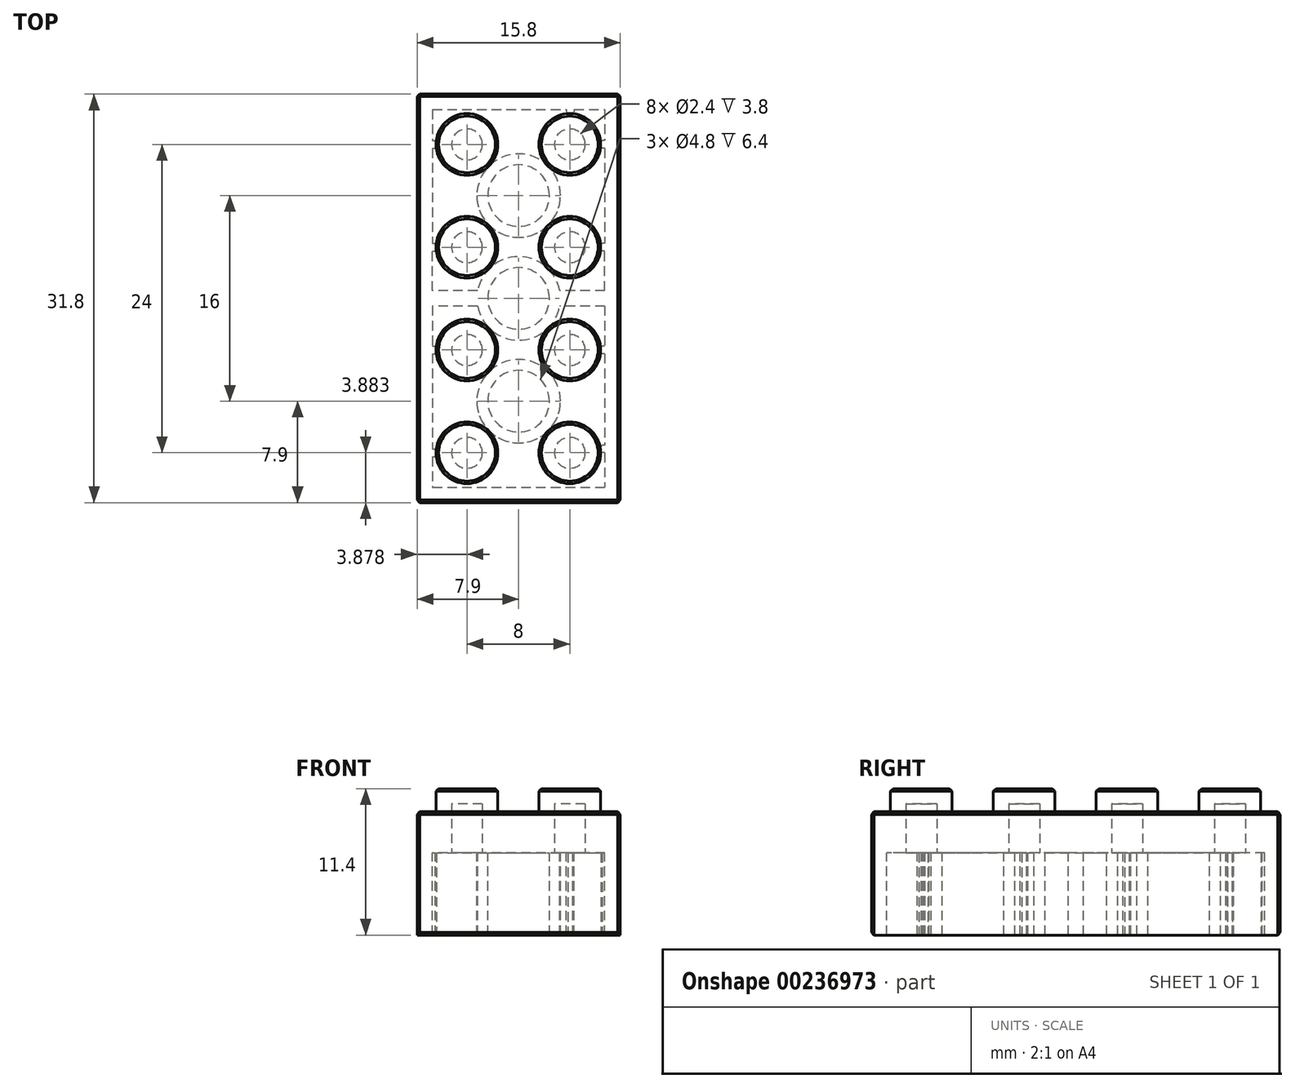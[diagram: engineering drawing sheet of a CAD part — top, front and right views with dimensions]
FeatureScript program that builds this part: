
annotation { "Feature Type Name" : "Feature", "Feature Type Description" : "" }
export const myFeature = defineFeature(function(context is Context, id is Id, definition is map)
    precondition{}
    {
        {
            var Q0;
            Q0=qCreatedBy(makeId("Top.planeOp"),FACE);
            var sketch = newSketch(context, id + "F0", { "sketchPlane" : qUnion([Q0])});
            skLineSegment(sketch, "E0.bottom", {"start": v(-7.9, 15.9) * mm, "end": v(7.9, 15.9) * mm});
            skLineSegment(sketch, "E0.top", {"start": v(-7.9, -15.9) * mm, "end": v(7.9, -15.9) * mm});
            skLineSegment(sketch, "E0.left", {"start": v(-7.9, 15.9) * mm, "end": v(-7.9, -15.9) * mm});
            skLineSegment(sketch, "E0.right", {"start": v(7.9, 15.9) * mm, "end": v(7.9, -15.9) * mm});
            skPoint(sketch, "E0.middle", {"position": v(0, 0) * mm});
            skSolve(sketch);
        }
        {
            var Q0;
            Q0=qCreatedBy(makeId("Top.planeOp"),FACE);
            var sketch = newSketch(context, id + "F1", { "sketchPlane" : qUnion([Q0])});
            skCircle(sketch, "E1", {"center": v(-4.02, 11.98) * mm, "radius": 2.4 * mm});
            skCircle(sketch, "E2", {"center": v(-4.02, 3.98) * mm, "radius": 2.4 * mm});
            skCircle(sketch, "E3", {"center": v(-4.02, -4.02) * mm, "radius": 2.4 * mm});
            skCircle(sketch, "E4", {"center": v(-4.02, -12.02) * mm, "radius": 2.4 * mm});
            skCircle(sketch, "E5", {"center": v(3.98, -12.02) * mm, "radius": 2.4 * mm});
            skCircle(sketch, "E6", {"center": v(3.98, -4.02) * mm, "radius": 2.4 * mm});
            skCircle(sketch, "E7", {"center": v(3.98, 3.98) * mm, "radius": 2.4 * mm});
            skCircle(sketch, "E8", {"center": v(3.98, 11.98) * mm, "radius": 2.4 * mm});
            skLineSegment(sketch, "E9", {"start": v(-4.02, 3.98) * mm, "end": v(3.98, 3.98) * mm});
            skLineSegment(sketch, "E10", {"start": v(0, 3.98) * mm, "end": v(0, 11.98) * mm});
            skSolve(sketch);
        }
        {
            var Q0;
            Q0=makeQuery(id+"F0.imprint","IMPRINT",FACE,{"disambiguationData":[TD([[makeQuery(id+"F0.imprint","IMPRINT",EDGE,{"derivedFrom":sQuery(id+"F0.wireOp",EDGE,"E0.bottom")}),-1.0]])]});
            extrude(context, id + "F2", {"entities" : qUnion([Q0]), "oppositeDirection" : true, "depth" : 9.6 * mm});
        }
        {
            var Q0;
            Q0=makeQuery(id+"F1.imprint","IMPRINT",FACE,{"disambiguationData":[TD([[makeQuery(id+"F1.imprint","IMPRINT",EDGE,{"derivedFrom":sQuery(id+"F1.wireOp",EDGE,"E1")}),1.0]])]});
            extrude(context, id + "F3", {"entities" : qUnion([Q0]), "operationType" : NewBodyOperationType.ADD, "depth" : 1.8 * mm});
        }
        {
            var Q0;
            Q0 = qSketchRegion(id + "F1", true);
            extrude(context, id + "F4", {"entities" : qUnion([Q0]), "operationType" : NewBodyOperationType.ADD, "depth" : 1.8 * mm});
        }
        {
            var Q0;
            Q0=makeQuery(id+"F2.opExtrude","CAP_FACE",FACE,{"disambiguationData":[OSD([sQuery(id+"F0.wireOp",EDGE,"E0.bottom"),sQuery(id+"F0.wireOp",EDGE,"E0.top"),sQuery(id+"F0.wireOp",EDGE,"E0.left"),sQuery(id+"F0.wireOp",EDGE,"E0.right")])],"isStart":false});
            shell(context, id + "F5", {"entities" : qUnion([Q0]), "thickness" : 1.2 * mm});
        }
        {
            var Q0;
            Q0=makeQuery(id+"F5.opShell","OFFSET_FACE",FACE,{"disambiguationData":[OSD([sQuery(id+"F0.wireOp",EDGE,"E0.bottom"),sQuery(id+"F0.wireOp",EDGE,"E0.top"),sQuery(id+"F0.wireOp",EDGE,"E0.left"),sQuery(id+"F0.wireOp",EDGE,"E0.right")])]});
            extrude(context, id + "F6", {"entities" : qUnion([Q0]), "operationType" : NewBodyOperationType.ADD, "depth" : 2 * mm});
        }
        {
            var Q0;
            Q0=makeQuery(id+"F6.opExtrude","CAP_FACE",FACE,{"disambiguationData":[OSD([sQuery(id+"F0.wireOp",EDGE,"E0.bottom"),sQuery(id+"F0.wireOp",EDGE,"E0.top"),sQuery(id+"F0.wireOp",EDGE,"E0.left"),sQuery(id+"F0.wireOp",EDGE,"E0.right")])],"isStart":false});
            var sketch = newSketch(context, id + "F7", { "sketchPlane" : qUnion([Q0])});
            skCircle(sketch, "E11", {"center": v(0, 8) * mm, "radius": 3.25 * mm});
            skCircle(sketch, "E12", {"center": v(0, 0) * mm, "radius": 3.25 * mm});
            skCircle(sketch, "E13", {"center": v(0, -8) * mm, "radius": 3.25 * mm});
            skCircle(sketch, "E14", {"center": v(0, 8) * mm, "radius": 2.4 * mm});
            skCircle(sketch, "E15", {"center": v(0, 0) * mm, "radius": 2.4 * mm});
            skCircle(sketch, "E16", {"center": v(0, -8) * mm, "radius": 2.4 * mm});
            skLineSegment(sketch, "E17", {"start": v(-6.7, -3.98) * mm, "end": v(-6.7, -3.68) * mm});
            skLineSegment(sketch, "E18", {"start": v(-6.7, -3.68) * mm, "end": v(-6.7, -3.98) * mm});
            skLineSegment(sketch, "E19", {"start": v(-6.7, -3.98) * mm, "end": v(-6.7, -4.28) * mm});
            skLineSegment(sketch, "E20", {"start": v(-6.7, 4.02) * mm, "end": v(-6.7, 4.32) * mm});
            skLineSegment(sketch, "E21", {"start": v(-6.7, 4.02) * mm, "end": v(-6.7, 3.72) * mm});
            skLineSegment(sketch, "E22", {"start": v(-6.7, 12.02) * mm, "end": v(-6.7, 11.72) * mm});
            skLineSegment(sketch, "E23", {"start": v(-6.7, -11.98) * mm, "end": v(-6.7, -11.68) * mm});
            skLineSegment(sketch, "E24", {"start": v(-6.7, -11.68) * mm, "end": v(-6.7, -12.28) * mm});
            skLineSegment(sketch, "E25", {"start": v(-3.98, -14.7) * mm, "end": v(-4.28, -14.7) * mm});
            skLineSegment(sketch, "E26", {"start": v(-3.98, -14.7) * mm, "end": v(4.02, -14.7) * mm});
            skLineSegment(sketch, "E27", {"start": v(4.02, -14.7) * mm, "end": v(3.72, -14.7) * mm});
            skLineSegment(sketch, "E28", {"start": v(3.72, -14.7) * mm, "end": v(4.02, -14.7) * mm});
            skLineSegment(sketch, "E29", {"start": v(6.7, -3.98) * mm, "end": v(6.7, -4.28) * mm});
            skLineSegment(sketch, "E30", {"start": v(6.7, -4.28) * mm, "end": v(6.7, -3.98) * mm});
            skLineSegment(sketch, "E31", {"start": v(6.7, -4.28) * mm, "end": v(6.7, -3.68) * mm});
            skLineSegment(sketch, "E32", {"start": v(6.7, -3.98) * mm, "end": v(6.7, 4.02) * mm});
            skLineSegment(sketch, "E33", {"start": v(6.7, 4.02) * mm, "end": v(6.7, 4.32) * mm});
            skLineSegment(sketch, "E34", {"start": v(6.7, 4.32) * mm, "end": v(6.7, 3.72) * mm});
            skLineSegment(sketch, "E35", {"start": v(6.7, 3.72) * mm, "end": v(6.7, 11.72) * mm});
            skLineSegment(sketch, "E36", {"start": v(6.7, 11.72) * mm, "end": v(6.4, 11.72) * mm});
            skLineSegment(sketch, "E37", {"start": v(6.7, 11.72) * mm, "end": v(6.7, 11.42) * mm});
            skLineSegment(sketch, "E38", {"start": v(6.7, 11.72) * mm, "end": v(6.7, 12.02) * mm});
            skLineSegment(sketch, "E39", {"start": v(-6.7, 14.7) * mm, "end": v(-3.98, 14.7) * mm});
            skLineSegment(sketch, "E40", {"start": v(-3.98, 14.7) * mm, "end": v(-3.68, 14.7) * mm});
            skLineSegment(sketch, "E41", {"start": v(-3.98, 14.7) * mm, "end": v(-4.28, 14.7) * mm});
            skLineSegment(sketch, "E42", {"start": v(-3.98, 14.7) * mm, "end": v(3.91, 14.7) * mm});
            skLineSegment(sketch, "E43", {"start": v(6.7, -11.98) * mm, "end": v(6.7, -11.68) * mm});
            skLineSegment(sketch, "E44", {"start": v(6.7, -11.98) * mm, "end": v(6.7, -12.28) * mm});
            skLineSegment(sketch, "E45", {"start": v(-6.7, 12.02) * mm, "end": v(-6.7, 12.32) * mm});
            skLineSegment(sketch, "E46.bottom", {"start": v(-6.7, 11.72) * mm, "end": v(-6.4, 11.72) * mm});
            skLineSegment(sketch, "E46.top", {"start": v(-6.7, 12.32) * mm, "end": v(-6.4, 12.32) * mm});
            skLineSegment(sketch, "E46.left", {"start": v(-6.7, 11.72) * mm, "end": v(-6.7, 12.32) * mm});
            skLineSegment(sketch, "E46.right", {"start": v(-6.4, 11.72) * mm, "end": v(-6.4, 12.32) * mm});
            skLineSegment(sketch, "E47.bottom", {"start": v(-6.7, 4.32) * mm, "end": v(-6.4, 4.32) * mm});
            skLineSegment(sketch, "E47.top", {"start": v(-6.7, 3.72) * mm, "end": v(-6.4, 3.72) * mm});
            skLineSegment(sketch, "E47.left", {"start": v(-6.7, 4.32) * mm, "end": v(-6.7, 3.72) * mm});
            skLineSegment(sketch, "E47.right", {"start": v(-6.4, 4.32) * mm, "end": v(-6.4, 3.72) * mm});
            skLineSegment(sketch, "E48.bottom", {"start": v(-6.7, -3.68) * mm, "end": v(-6.4, -3.68) * mm});
            skLineSegment(sketch, "E48.top", {"start": v(-6.7, -4.28) * mm, "end": v(-6.4, -4.28) * mm});
            skLineSegment(sketch, "E48.left", {"start": v(-6.7, -3.68) * mm, "end": v(-6.7, -4.28) * mm});
            skLineSegment(sketch, "E48.right", {"start": v(-6.4, -3.68) * mm, "end": v(-6.4, -4.28) * mm});
            skLineSegment(sketch, "E49.bottom", {"start": v(-6.7, -11.68) * mm, "end": v(-6.7, -11.68) * mm});
            skLineSegment(sketch, "E49.top", {"start": v(-6.7, -12.28) * mm, "end": v(-6.7, -12.28) * mm});
            skLineSegment(sketch, "E50.bottom", {"start": v(-6.7, -11.68) * mm, "end": v(-6.4, -11.68) * mm});
            skLineSegment(sketch, "E50.top", {"start": v(-6.7, -12.28) * mm, "end": v(-6.4, -12.28) * mm});
            skLineSegment(sketch, "E50.right", {"start": v(-6.4, -11.68) * mm, "end": v(-6.4, -12.28) * mm});
            skLineSegment(sketch, "E51.bottom", {"start": v(-4.28, -14.7) * mm, "end": v(-3.68, -14.7) * mm});
            skLineSegment(sketch, "E51.top", {"start": v(-4.28, -14.4) * mm, "end": v(-3.68, -14.4) * mm});
            skLineSegment(sketch, "E51.left", {"start": v(-4.28, -14.7) * mm, "end": v(-4.28, -14.4) * mm});
            skLineSegment(sketch, "E51.right", {"start": v(-3.68, -14.7) * mm, "end": v(-3.68, -14.4) * mm});
            skLineSegment(sketch, "E52.bottom", {"start": v(3.72, -14.7) * mm, "end": v(4.32, -14.7) * mm});
            skLineSegment(sketch, "E52.top", {"start": v(3.72, -14.4) * mm, "end": v(4.32, -14.4) * mm});
            skLineSegment(sketch, "E52.left", {"start": v(3.72, -14.7) * mm, "end": v(3.72, -14.4) * mm});
            skLineSegment(sketch, "E52.right", {"start": v(4.32, -14.7) * mm, "end": v(4.32, -14.4) * mm});
            skLineSegment(sketch, "E53.bottom", {"start": v(6.7, -11.68) * mm, "end": v(6.4, -11.68) * mm});
            skLineSegment(sketch, "E53.top", {"start": v(6.7, -12.28) * mm, "end": v(6.4, -12.28) * mm});
            skLineSegment(sketch, "E53.left", {"start": v(6.7, -11.68) * mm, "end": v(6.7, -12.28) * mm});
            skLineSegment(sketch, "E53.right", {"start": v(6.4, -11.68) * mm, "end": v(6.4, -12.28) * mm});
            skLineSegment(sketch, "E54.bottom", {"start": v(6.7, -3.68) * mm, "end": v(6.4, -3.68) * mm});
            skLineSegment(sketch, "E54.top", {"start": v(6.7, -4.28) * mm, "end": v(6.4, -4.28) * mm});
            skLineSegment(sketch, "E54.left", {"start": v(6.7, -3.68) * mm, "end": v(6.7, -4.28) * mm});
            skLineSegment(sketch, "E54.right", {"start": v(6.4, -3.68) * mm, "end": v(6.4, -4.28) * mm});
            skLineSegment(sketch, "E55.bottom", {"start": v(6.7, 3.72) * mm, "end": v(6.4, 3.72) * mm});
            skLineSegment(sketch, "E55.top", {"start": v(6.7, 4.32) * mm, "end": v(6.4, 4.32) * mm});
            skLineSegment(sketch, "E55.left", {"start": v(6.7, 3.72) * mm, "end": v(6.7, 4.32) * mm});
            skLineSegment(sketch, "E55.right", {"start": v(6.4, 3.72) * mm, "end": v(6.4, 4.32) * mm});
            skLineSegment(sketch, "E56.bottom", {"start": v(6.7, 12.02) * mm, "end": v(6.4, 12.02) * mm});
            skLineSegment(sketch, "E56.top", {"start": v(6.7, 11.42) * mm, "end": v(6.4, 11.42) * mm});
            skLineSegment(sketch, "E56.left", {"start": v(6.7, 12.02) * mm, "end": v(6.7, 11.42) * mm});
            skLineSegment(sketch, "E56.right", {"start": v(6.4, 12.02) * mm, "end": v(6.4, 11.42) * mm});
            skLineSegment(sketch, "E57.bottom", {"start": v(3.91, 14.7) * mm, "end": v(3.61, 14.7) * mm});
            skLineSegment(sketch, "E57.top", {"start": v(3.91, 14.4) * mm, "end": v(3.61, 14.4) * mm});
            skLineSegment(sketch, "E57.right", {"start": v(3.61, 14.7) * mm, "end": v(3.61, 14.4) * mm});
            skLineSegment(sketch, "E58.bottom", {"start": v(3.91, 14.7) * mm, "end": v(4.21, 14.7) * mm});
            skLineSegment(sketch, "E58.top", {"start": v(3.91, 14.4) * mm, "end": v(4.21, 14.4) * mm});
            skLineSegment(sketch, "E58.right", {"start": v(4.21, 14.7) * mm, "end": v(4.21, 14.4) * mm});
            skLineSegment(sketch, "E59.bottom", {"start": v(-4.28, 14.7) * mm, "end": v(-3.68, 14.7) * mm});
            skLineSegment(sketch, "E59.top", {"start": v(-4.28, 14.4) * mm, "end": v(-3.68, 14.4) * mm});
            skLineSegment(sketch, "E59.left", {"start": v(-4.28, 14.7) * mm, "end": v(-4.28, 14.4) * mm});
            skLineSegment(sketch, "E59.right", {"start": v(-3.68, 14.7) * mm, "end": v(-3.68, 14.4) * mm});
            skSolve(sketch);
        }
        {
            var Q0;
            Q0=makeQuery(id+"F7.imprint","IMPRINT",FACE,{"disambiguationData":[TD([[makeQuery(id+"F7.imprint","IMPRINT",EDGE,{"derivedFrom":sQuery(id+"F7.wireOp",EDGE,"E11")}),1.0]])]});
            var Q1;
            Q1=makeQuery(id+"F7.imprint","IMPRINT",FACE,{"disambiguationData":[TD([[makeQuery(id+"F7.imprint","IMPRINT",EDGE,{"derivedFrom":sQuery(id+"F7.wireOp",EDGE,"E12")}),1.0]])]});
            var Q2;
            Q2=makeQuery(id+"F7.imprint","IMPRINT",FACE,{"disambiguationData":[TD([[makeQuery(id+"F7.imprint","IMPRINT",EDGE,{"derivedFrom":sQuery(id+"F7.wireOp",EDGE,"E13")}),1.0]])]});
            extrude(context, id + "F8", {"entities" : qUnion([Q0, Q1, Q2]), "operationType" : NewBodyOperationType.ADD, "depth" : 6.4 * mm});
        }
        {
            var Q0;
            Q0=makeQuery(id+"F7.imprint","IMPRINT",FACE,{"disambiguationData":[TD([[makeQuery(id+"F7.imprint","IMPRINT",EDGE,{"derivedFrom":sQuery(id+"F7.wireOp",EDGE,"E59.bottom")}),-1.0]])]});
            var Q1;
            Q1=makeQuery(id+"F7.imprint","IMPRINT",FACE,{"disambiguationData":[TD([[makeQuery(id+"F7.imprint","IMPRINT",EDGE,{"derivedFrom":sQuery(id+"F7.wireOp",EDGE,"E57.bottom")}),-1.0]])]});
            var Q2;
            Q2=makeQuery(id+"F7.imprint","IMPRINT",FACE,{"disambiguationData":[TD([[makeQuery(id+"F7.imprint","IMPRINT",EDGE,{"derivedFrom":sQuery(id+"F7.wireOp",EDGE,"E46.bottom")}),1.0]])]});
            var Q3;
            Q3=makeQuery(id+"F7.imprint","IMPRINT",FACE,{"disambiguationData":[TD([[makeQuery(id+"F7.imprint","IMPRINT",EDGE,{"derivedFrom":sQuery(id+"F7.wireOp",EDGE,"E47.bottom")}),-1.0]])]});
            var Q4;
            {var subQ0=sQuery(id+"F7.wireOp",EDGE,"E48.bottom");Q4=makeQuery(id+"F7.imprint","IMPRINT",FACE,{"disambiguationData":[TD([[makeQuery(id+"F7.imprint","IMPRINT",EDGE,{"derivedFrom":subQ0}),-1.0]])]});}
            var Q5;
            {var subQ0=sQuery(id+"F7.wireOp",EDGE,"E50.bottom");Q5=makeQuery(id+"F7.imprint","IMPRINT",FACE,{"disambiguationData":[TD([[makeQuery(id+"F7.imprint","IMPRINT",EDGE,{"derivedFrom":subQ0}),-1.0]])]});}
            var Q6;
            Q6=makeQuery(id+"F7.imprint","IMPRINT",FACE,{"disambiguationData":[TD([[makeQuery(id+"F7.imprint","IMPRINT",EDGE,{"derivedFrom":sQuery(id+"F7.wireOp",EDGE,"E51.bottom")}),1.0]])]});
            var Q7;
            {var subQ0=sQuery(id+"F7.wireOp",EDGE,"E36");Q7=makeQuery(id+"F7.imprint","IMPRINT",FACE,{"disambiguationData":[TD([[makeQuery(id+"F7.imprint","IMPRINT",EDGE,{"derivedFrom":subQ0}),1.0]])]});}
            var Q8;
            {var subQ0=sQuery(id+"F7.wireOp",EDGE,"E36");Q8=makeQuery(id+"F7.imprint","IMPRINT",FACE,{"disambiguationData":[TD([[makeQuery(id+"F7.imprint","IMPRINT",EDGE,{"derivedFrom":subQ0}),-1.0]])]});}
            var Q9;
            Q9=makeQuery(id+"F7.imprint","IMPRINT",FACE,{"disambiguationData":[TD([[makeQuery(id+"F7.imprint","IMPRINT",EDGE,{"derivedFrom":sQuery(id+"F7.wireOp",EDGE,"E55.bottom")}),-1.0]])]});
            var Q10;
            {var subQ0=sQuery(id+"F7.wireOp",EDGE,"E54.bottom");Q10=makeQuery(id+"F7.imprint","IMPRINT",FACE,{"disambiguationData":[TD([[makeQuery(id+"F7.imprint","IMPRINT",EDGE,{"derivedFrom":subQ0}),1.0]])]});}
            var Q11;
            Q11=makeQuery(id+"F7.imprint","IMPRINT",FACE,{"disambiguationData":[TD([[makeQuery(id+"F7.imprint","IMPRINT",EDGE,{"derivedFrom":sQuery(id+"F7.wireOp",EDGE,"E52.top")}),-1.0]])]});
            var Q12;
            Q12=makeQuery(id+"F7.imprint","IMPRINT",FACE,{"disambiguationData":[TD([[makeQuery(id+"F7.imprint","IMPRINT",EDGE,{"derivedFrom":sQuery(id+"F7.wireOp",EDGE,"E53.bottom")}),1.0]])]});
            extrude(context, id + "F9", {"entities" : qUnion([Q0, Q1, Q2, Q3, Q4, Q5, Q6, Q7, Q8, Q9, Q10, Q11, Q12]), "operationType" : NewBodyOperationType.ADD, "depth" : 6.4 * mm});
        }
        {
            var Q0;
            Q0=makeQuery(id+"F9.opExtrude","SWEPT_EDGE",EDGE,{"disambiguationData":[OSD([sQuery(id+"F7.wireOp",EDGE,"E56.bottom"),sQuery(id+"F7.wireOp",EDGE,"E56.right")])]});
            var Q1;
            Q1=makeQuery(id+"F9.opExtrude","SWEPT_EDGE",EDGE,{"disambiguationData":[OSD([sQuery(id+"F7.wireOp",EDGE,"E56.top"),sQuery(id+"F7.wireOp",EDGE,"E56.right")])]});
            var Q2;
            Q2=makeQuery(id+"F9.opExtrude","SWEPT_EDGE",EDGE,{"disambiguationData":[OSD([sQuery(id+"F7.wireOp",EDGE,"E55.top"),sQuery(id+"F7.wireOp",EDGE,"E55.right")])]});
            var Q3;
            Q3=makeQuery(id+"F9.opExtrude","SWEPT_EDGE",EDGE,{"disambiguationData":[OSD([sQuery(id+"F7.wireOp",EDGE,"E55.bottom"),sQuery(id+"F7.wireOp",EDGE,"E55.right")])]});
            var Q4;
            Q4=makeQuery(id+"F9.opExtrude","SWEPT_EDGE",EDGE,{"disambiguationData":[OSD([sQuery(id+"F7.wireOp",EDGE,"E54.bottom"),sQuery(id+"F7.wireOp",EDGE,"E54.right")])]});
            var Q5;
            Q5=makeQuery(id+"F9.opExtrude","SWEPT_EDGE",EDGE,{"disambiguationData":[OSD([sQuery(id+"F7.wireOp",EDGE,"E54.top"),sQuery(id+"F7.wireOp",EDGE,"E54.right")])]});
            var Q6;
            Q6=makeQuery(id+"F9.opExtrude","SWEPT_EDGE",EDGE,{"disambiguationData":[OSD([sQuery(id+"F7.wireOp",EDGE,"E53.bottom"),sQuery(id+"F7.wireOp",EDGE,"E53.right")])]});
            var Q7;
            Q7=makeQuery(id+"F9.opExtrude","SWEPT_EDGE",EDGE,{"disambiguationData":[OSD([sQuery(id+"F7.wireOp",EDGE,"E53.top"),sQuery(id+"F7.wireOp",EDGE,"E53.right")])]});
            var Q8;
            Q8=makeQuery(id+"F9.opExtrude","SWEPT_EDGE",EDGE,{"disambiguationData":[OSD([sQuery(id+"F7.wireOp",EDGE,"E46.top"),sQuery(id+"F7.wireOp",EDGE,"E46.right")])]});
            var Q9;
            Q9=makeQuery(id+"F9.opExtrude","SWEPT_EDGE",EDGE,{"disambiguationData":[OSD([sQuery(id+"F7.wireOp",EDGE,"E46.bottom"),sQuery(id+"F7.wireOp",EDGE,"E46.right")])]});
            var Q10;
            Q10=makeQuery(id+"F9.opExtrude","SWEPT_EDGE",EDGE,{"disambiguationData":[OSD([sQuery(id+"F7.wireOp",EDGE,"E47.bottom"),sQuery(id+"F7.wireOp",EDGE,"E47.right")])]});
            var Q11;
            Q11=makeQuery(id+"F9.opExtrude","SWEPT_EDGE",EDGE,{"disambiguationData":[OSD([sQuery(id+"F7.wireOp",EDGE,"E47.top"),sQuery(id+"F7.wireOp",EDGE,"E47.right")])]});
            var Q12;
            Q12=makeQuery(id+"F9.opExtrude","SWEPT_EDGE",EDGE,{"disambiguationData":[OSD([sQuery(id+"F7.wireOp",EDGE,"E48.bottom"),sQuery(id+"F7.wireOp",EDGE,"E48.right")])]});
            var Q13;
            Q13=makeQuery(id+"F9.opExtrude","SWEPT_EDGE",EDGE,{"disambiguationData":[OSD([sQuery(id+"F7.wireOp",EDGE,"E48.top"),sQuery(id+"F7.wireOp",EDGE,"E48.right")])]});
            var Q14;
            Q14=makeQuery(id+"F9.opExtrude","SWEPT_EDGE",EDGE,{"disambiguationData":[OSD([sQuery(id+"F7.wireOp",EDGE,"E50.bottom"),sQuery(id+"F7.wireOp",EDGE,"E50.right")])]});
            var Q15;
            Q15=makeQuery(id+"F9.opExtrude","SWEPT_EDGE",EDGE,{"disambiguationData":[OSD([sQuery(id+"F7.wireOp",EDGE,"E50.top"),sQuery(id+"F7.wireOp",EDGE,"E50.right")])]});
            var Q16;
            Q16=makeQuery(id+"F9.opExtrude","SWEPT_EDGE",EDGE,{"disambiguationData":[OSD([sQuery(id+"F7.wireOp",EDGE,"E51.top"),sQuery(id+"F7.wireOp",EDGE,"E51.right")])]});
            var Q17;
            Q17=makeQuery(id+"F9.opExtrude","SWEPT_EDGE",EDGE,{"disambiguationData":[OSD([sQuery(id+"F7.wireOp",EDGE,"E51.top"),sQuery(id+"F7.wireOp",EDGE,"E51.left")])]});
            var Q18;
            Q18=makeQuery(id+"F9.opExtrude","SWEPT_EDGE",EDGE,{"disambiguationData":[OSD([sQuery(id+"F7.wireOp",EDGE,"E52.top"),sQuery(id+"F7.wireOp",EDGE,"E52.left")])]});
            var Q19;
            Q19=makeQuery(id+"F9.opExtrude","SWEPT_EDGE",EDGE,{"disambiguationData":[OSD([sQuery(id+"F7.wireOp",EDGE,"E52.top"),sQuery(id+"F7.wireOp",EDGE,"E52.right")])]});
            var Q20;
            Q20=makeQuery(id+"F9.opExtrude","SWEPT_EDGE",EDGE,{"disambiguationData":[OSD([sQuery(id+"F7.wireOp",EDGE,"E59.top"),sQuery(id+"F7.wireOp",EDGE,"E59.right")])]});
            var Q21;
            Q21=makeQuery(id+"F9.opExtrude","SWEPT_EDGE",EDGE,{"disambiguationData":[OSD([sQuery(id+"F7.wireOp",EDGE,"E59.top"),sQuery(id+"F7.wireOp",EDGE,"E59.left")])]});
            var Q22;
            Q22=makeQuery(id+"F9.opExtrude","SWEPT_EDGE",EDGE,{"disambiguationData":[OSD([sQuery(id+"F7.wireOp",EDGE,"E58.top"),sQuery(id+"F7.wireOp",EDGE,"E58.right")])]});
            var Q23;
            Q23=makeQuery(id+"F9.opExtrude","SWEPT_EDGE",EDGE,{"disambiguationData":[OSD([sQuery(id+"F7.wireOp",EDGE,"E57.top"),sQuery(id+"F7.wireOp",EDGE,"E57.right")])]});
            chamfer(context, id + "F10", {"entities" : qUnion([Q0, Q1, Q2, Q3, Q4, Q5, Q6, Q7, Q8, Q9, Q10, Q11, Q12, Q13, Q14, Q15, Q16, Q17, Q18, Q19, Q20, Q21, Q22, Q23]), "width" : 0.1 * mm, "tangentPropagation" : true});
        }
        {
            var Q0;
            Q0=makeQuery(id+"F2.opExtrude","CAP_EDGE",EDGE,{"disambiguationData":[OSD([sQuery(id+"F0.wireOp",EDGE,"E0.top")])],"isStart":true});
            var Q1;
            Q1=makeQuery(id+"F2.opExtrude","SWEPT_EDGE",EDGE,{"disambiguationData":[OSD([sQuery(id+"F0.wireOp",EDGE,"E0.top"),sQuery(id+"F0.wireOp",EDGE,"E0.left")])]});
            var Q2;
            Q2=makeQuery(id+"F2.opExtrude","SWEPT_EDGE",EDGE,{"disambiguationData":[OSD([sQuery(id+"F0.wireOp",EDGE,"E0.top"),sQuery(id+"F0.wireOp",EDGE,"E0.right")])]});
            var Q3;
            Q3=makeQuery(id+"F2.opExtrude","CAP_EDGE",EDGE,{"disambiguationData":[OSD([sQuery(id+"F0.wireOp",EDGE,"E0.right")])],"isStart":true});
            var Q4;
            Q4=makeQuery(id+"F2.opExtrude","CAP_EDGE",EDGE,{"disambiguationData":[OSD([sQuery(id+"F0.wireOp",EDGE,"E0.left")])],"isStart":true});
            var Q5;
            Q5=makeQuery(id+"F4.opExtrude","CAP_EDGE",EDGE,{"disambiguationData":[OSD([sQuery(id+"F1.wireOp",EDGE,"E4")])],"isStart":false});
            var Q6;
            Q6=makeQuery(id+"F4.opExtrude","CAP_EDGE",EDGE,{"disambiguationData":[OSD([sQuery(id+"F1.wireOp",EDGE,"E5")])],"isStart":false});
            var Q7;
            Q7=makeQuery(id+"F4.opExtrude","CAP_EDGE",EDGE,{"disambiguationData":[OSD([sQuery(id+"F1.wireOp",EDGE,"E6")])],"isStart":false});
            var Q8;
            Q8=makeQuery(id+"F4.opExtrude","CAP_EDGE",EDGE,{"disambiguationData":[OSD([sQuery(id+"F1.wireOp",EDGE,"E3")])],"isStart":false});
            var Q9;
            Q9=makeQuery(id+"F4.opExtrude","CAP_EDGE",EDGE,{"disambiguationData":[OSD([sQuery(id+"F1.wireOp",EDGE,"E2")])],"isStart":false});
            var Q10;
            Q10=makeQuery(id+"F4.opExtrude","CAP_EDGE",EDGE,{"disambiguationData":[OSD([sQuery(id+"F1.wireOp",EDGE,"E7")])],"isStart":false});
            var Q11;
            Q11=makeQuery(id+"F4.opExtrude","CAP_EDGE",EDGE,{"disambiguationData":[OSD([sQuery(id+"F1.wireOp",EDGE,"E8")])],"isStart":false});
            var Q12;
            Q12=makeQuery(id+"F3.opExtrude","CAP_EDGE",EDGE,{"disambiguationData":[OSD([sQuery(id+"F1.wireOp",EDGE,"E1")])],"isStart":false});
            var Q13;
            Q13=makeQuery(id+"F2.opExtrude","CAP_EDGE",EDGE,{"disambiguationData":[OSD([sQuery(id+"F0.wireOp",EDGE,"E0.bottom")])],"isStart":false});
            var Q14;
            Q14=makeQuery(id+"F2.opExtrude","SWEPT_EDGE",EDGE,{"disambiguationData":[OSD([sQuery(id+"F0.wireOp",EDGE,"E0.bottom"),sQuery(id+"F0.wireOp",EDGE,"E0.left")])]});
            chamfer(context, id + "F11", {"entities" : qUnion([Q0, Q1, Q2, Q3, Q4, Q5, Q6, Q7, Q8, Q9, Q10, Q11, Q12, Q13, Q14]), "width" : 0.2 * mm, "tangentPropagation" : true});
        }
        {
            var Q0;
            Q0=makeQuery(id+"F2.opExtrude","CAP_EDGE",EDGE,{"disambiguationData":[OSD([sQuery(id+"F0.wireOp",EDGE,"E0.top")])],"isStart":false});
            chamfer(context, id + "F12", {"entities" : qUnion([Q0]), "width" : 0.2 * mm, "tangentPropagation" : true});
        }
        {
            var Q0;
            Q0=makeQuery(id+"F2.opExtrude","CAP_EDGE",EDGE,{"disambiguationData":[OSD([sQuery(id+"F0.wireOp",EDGE,"E0.bottom")])],"isStart":true});
            chamfer(context, id + "F13", {"entities" : qUnion([Q0]), "width" : .2 * mm, "tangentPropagation" : true});
        }
        {
            var Q0;
            Q0=makeQuery(id+"F2.opExtrude","SWEPT_EDGE",EDGE,{"disambiguationData":[OSD([sQuery(id+"F0.wireOp",EDGE,"E0.bottom"),sQuery(id+"F0.wireOp",EDGE,"E0.right")])]});
            chamfer(context, id + "F14", {"entities" : qUnion([Q0]), "width" : .2 * mm, "tangentPropagation" : true});
        }
        {
            var Q0;
            {var subQ1=sQuery(id+"F0.wireOp",EDGE,"E0.top");var subQ3=sQuery(id+"F0.wireOp",EDGE,"E0.right");var subQ9=sQuery(id+"F0.wireOp",EDGE,"E0.left");var subQ10=sQuery(id+"F0.wireOp",EDGE,"E0.bottom");Q0=makeQuery(id+"F8.boolean.opBoolean","SPLIT",FACE,{"disambiguationData":[TD([makeQuery(id+"F5.opShell","OFFSET_FACE",FACE,{"disambiguationData":[OSD([subQ10])]})])],"derivedFrom":makeQuery(id+"F6.opExtrude","CAP_FACE",FACE,{"disambiguationData":[OSD([subQ10,subQ1,subQ9,subQ3])],"isStart":false})});}
            var sketch = newSketch(context, id + "F15", { "sketchPlane" : qUnion([Q0])});
            skLineSegment(sketch, "E60.bottom", {"start": v(6.7, -0.6) * mm, "end": v(-6.7, -0.6) * mm});
            skLineSegment(sketch, "E60.top", {"start": v(6.7, 0.6) * mm, "end": v(-6.7, 0.6) * mm});
            skLineSegment(sketch, "E60.left", {"start": v(6.7, -0.6) * mm, "end": v(6.7, 0.6) * mm});
            skLineSegment(sketch, "E60.right", {"start": v(-6.7, -0.6) * mm, "end": v(-6.7, 0.6) * mm});
            skPoint(sketch, "E60.middle", {"position": v(0, 0) * mm});
            skSolve(sketch);
        }
        {
            var Q0;
            {var subQ0=sQuery(id+"F15.wireOp",EDGE,"E60.right");Q0=makeQuery(id+"F15.imprint","IMPRINT",FACE,{"disambiguationData":[TD([[makeQuery(id+"F15.imprint","IMPRINT",EDGE,{"derivedFrom":subQ0}),-1.0]])]});}
            var Q1;
            {var subQ0=sQuery(id+"F15.wireOp",EDGE,"E60.left");Q1=makeQuery(id+"F15.imprint","IMPRINT",FACE,{"disambiguationData":[TD([[makeQuery(id+"F15.imprint","IMPRINT",EDGE,{"derivedFrom":subQ0}),1.0]])]});}
            extrude(context, id + "F16", {"entities" : qUnion([Q0, Q1]), "operationType" : NewBodyOperationType.ADD, "depth" : 6.4 * mm});
        }
    });
